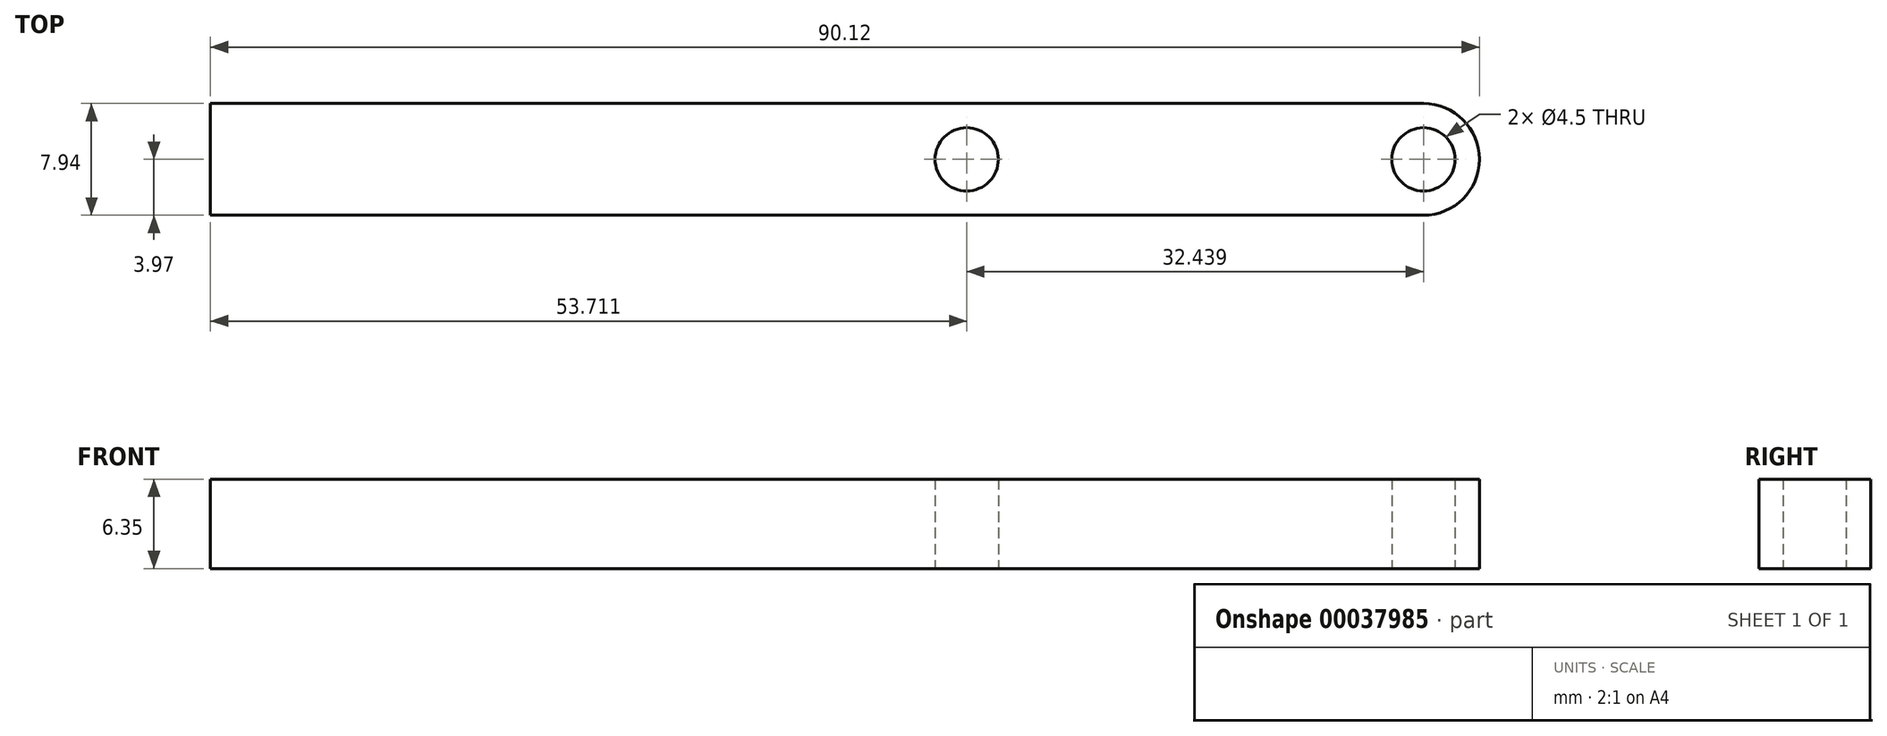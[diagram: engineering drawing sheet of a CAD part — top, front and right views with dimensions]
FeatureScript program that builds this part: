
annotation { "Feature Type Name" : "Feature", "Feature Type Description" : "" }
export const myFeature = defineFeature(function(context is Context, id is Id, definition is map)
    precondition{}
    {
        {
            var Q0;
            Q0=qCreatedBy(makeId("Top.planeOp"),FACE);
            var sketch = newSketch(context, id + "F0", { "sketchPlane" : qUnion([Q0])});
            skLineSegment(sketch, "E0", {"start": v(0, 0) * mm, "end": v(-32.44, 0) * mm, "construction": true});
            skCircle(sketch, "E1", {"center": v(-32.44, 0) * mm, "radius": 2.25 * mm});
            skCircle(sketch, "E2", {"center": v(0, 0) * mm, "radius": 2.25 * mm});
            skLineSegment(sketch, "E3.bottom", {"start": v(0, -3.97) * mm, "end": v(-86.15, -3.97) * mm});
            skLineSegment(sketch, "E3.top", {"start": v(0, 3.97) * mm, "end": v(-86.15, 3.97) * mm});
            skLineSegment(sketch, "E3.left", {"start": v(0, -3.97) * mm, "end": v(0, 3.97) * mm});
            skLineSegment(sketch, "E3.right", {"start": v(-86.15, -3.97) * mm, "end": v(-86.15, 3.97) * mm});
            skArc(sketch, "E4", {"start": v(0, -3.97) * mm, "mid": v(3.97, 0) * mm, "end": v(0, 3.97) * mm});
            skSolve(sketch);
        }
        {
            var Q0;
            Q0 = qSketchRegion(id + "F0", true);
            extrude(context, id + "F1", {"entities" : qUnion([Q0]), "depth" : 6.35 * mm});
        }
    });
